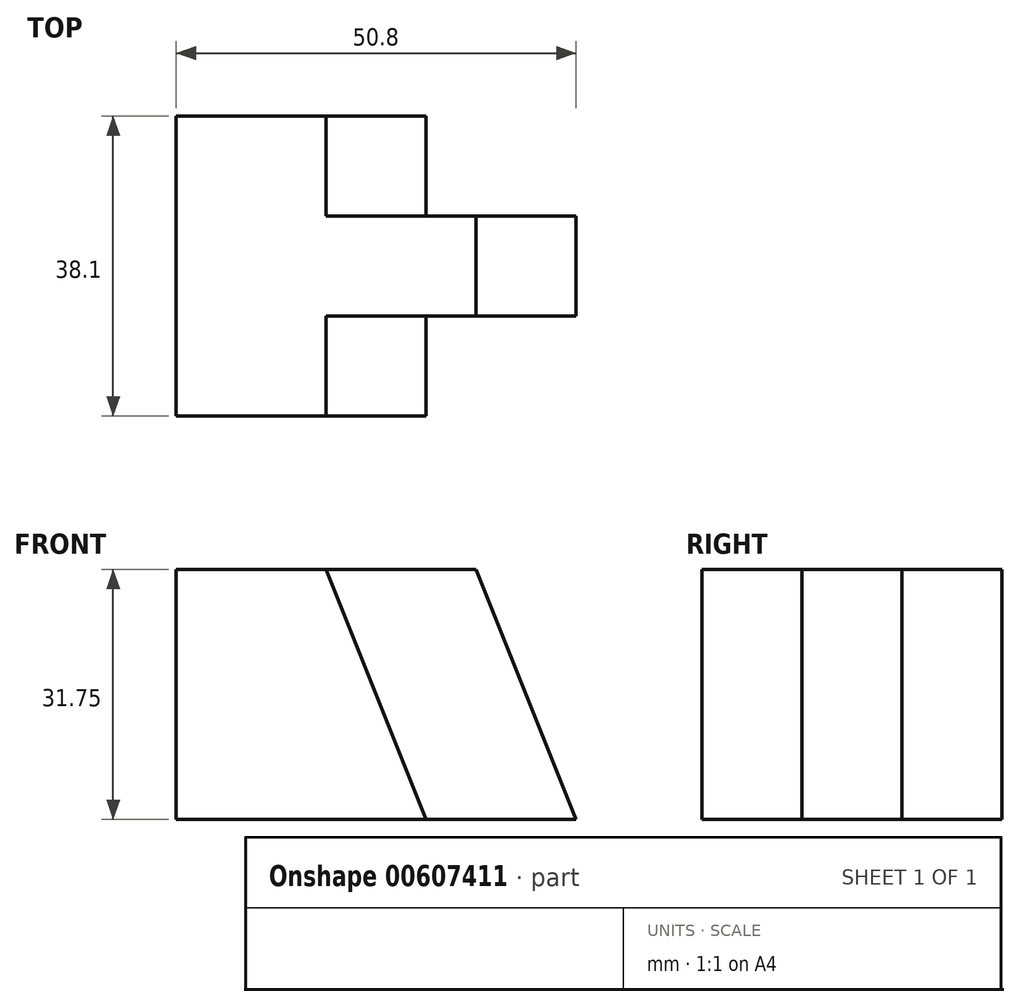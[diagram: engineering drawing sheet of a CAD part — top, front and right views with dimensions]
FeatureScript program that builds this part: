
annotation { "Feature Type Name" : "Feature", "Feature Type Description" : "" }
export const myFeature = defineFeature(function(context is Context, id is Id, definition is map)
    precondition{}
    {
        {
            var Q0;
            Q0=qCreatedBy(makeId("Right.planeOp"),FACE);
            var sketch = newSketch(context, id + "F0", { "sketchPlane" : qUnion([Q0])});
            skLineSegment(sketch, "E0", {"start": v(0, 0) * mm, "end": v(19.05, 0) * mm});
            skLineSegment(sketch, "E1", {"start": v(19.05, 0) * mm, "end": v(-19.05, 0) * mm});
            skLineSegment(sketch, "E2", {"start": v(-19.05, 0) * mm, "end": v(-19.05, -31.75) * mm});
            skLineSegment(sketch, "E3", {"start": v(-19.05, -31.75) * mm, "end": v(19.05, -31.75) * mm});
            skLineSegment(sketch, "E4", {"start": v(19.05, -31.75) * mm, "end": v(19.05, 0) * mm});
            skSolve(sketch);
        }
        {
            var Q0;
            Q0 = qSketchRegion(id + "F0", true);
            extrude(context, id + "F1", {"entities" : qUnion([Q0]), "depth" : 50.8 * mm, "offsetDistance" : 25.4 * mm});
        }
        {
            var Q0;
            Q0=makeQuery(id+"F1.opExtrude","CAP_FACE",FACE,{"disambiguationData":[OSD([sQuery(id+"F0.wireOp",EDGE,"E1"),sQuery(id+"F0.wireOp",EDGE,"E2"),sQuery(id+"F0.wireOp",EDGE,"E3"),sQuery(id+"F0.wireOp",EDGE,"E4")])],"isStart":false});
            var sketch = newSketch(context, id + "F2", { "sketchPlane" : qUnion([Q0])});
            skLineSegment(sketch, "E5", {"start": v(-19.05, 0) * mm, "end": v(-6.35, 0) * mm});
            skLineSegment(sketch, "E6", {"start": v(-6.35, 0) * mm, "end": v(-6.35, -31.75) * mm});
            skLineSegment(sketch, "E7", {"start": v(-6.35, -31.75) * mm, "end": v(-19.05, -31.75) * mm});
            skLineSegment(sketch, "E8", {"start": v(-19.05, -31.75) * mm, "end": v(-19.05, 0) * mm});
            skSolve(sketch);
        }
        {
            var Q0;
            Q0 = qSketchRegion(id + "F2", true);
            extrude(context, id + "F3", {"entities" : qUnion([Q0]), "operationType" : NewBodyOperationType.REMOVE, "oppositeDirection" : true, "depth" : 19.05 * mm, "offsetDistance" : 25.4 * mm});
        }
        {
            var Q0;
            Q0=makeQuery(id+"F1.opExtrude","SWEPT_FACE",FACE,{"disambiguationData":[OSD([sQuery(id+"F0.wireOp",EDGE,"E2")])]});
            var sketch = newSketch(context, id + "F4", { "sketchPlane" : qUnion([Q0])});
            skLineSegment(sketch, "E9", {"start": v(31.75, 0) * mm, "end": v(19.05, 0) * mm});
            skLineSegment(sketch, "E10", {"start": v(19.05, 0) * mm, "end": v(31.75, -31.75) * mm});
            skLineSegment(sketch, "E11", {"start": v(31.75, -31.75) * mm, "end": v(31.75, 0) * mm});
            skSolve(sketch);
        }
        {
            var Q0;
            Q0 = qSketchRegion(id + "F4", true);
            extrude(context, id + "F5", {"entities" : qUnion([Q0]), "operationType" : NewBodyOperationType.REMOVE, "oppositeDirection" : true, "depth" : 12.7 * mm, "offsetDistance" : 25.4 * mm});
        }
        {
            var Q0;
            Q0=makeQuery(id+"F1.opExtrude","CAP_FACE",FACE,{"disambiguationData":[OSD([sQuery(id+"F0.wireOp",EDGE,"E1"),sQuery(id+"F0.wireOp",EDGE,"E2"),sQuery(id+"F0.wireOp",EDGE,"E3"),sQuery(id+"F0.wireOp",EDGE,"E4")])],"isStart":false});
            var sketch = newSketch(context, id + "F6", { "sketchPlane" : qUnion([Q0])});
            skLineSegment(sketch, "E12", {"start": v(6.35, 0) * mm, "end": v(6.35, -31.75) * mm});
            skLineSegment(sketch, "E13", {"start": v(6.35, -31.75) * mm, "end": v(19.05, -31.75) * mm});
            skLineSegment(sketch, "E14", {"start": v(19.05, -31.75) * mm, "end": v(19.05, 0) * mm});
            skLineSegment(sketch, "E15", {"start": v(19.05, 0) * mm, "end": v(6.35, 0) * mm});
            skSolve(sketch);
        }
        {
            var Q0;
            Q0 = qSketchRegion(id + "F6", true);
            extrude(context, id + "F7", {"entities" : qUnion([Q0]), "operationType" : NewBodyOperationType.REMOVE, "oppositeDirection" : true, "depth" : 19.05 * mm, "offsetDistance" : 25.4 * mm});
        }
        {
            var Q0;
            Q0=makeQuery(id+"F1.opExtrude","SWEPT_FACE",FACE,{"disambiguationData":[OSD([sQuery(id+"F0.wireOp",EDGE,"E4")])]});
            var sketch = newSketch(context, id + "F8", { "sketchPlane" : qUnion([Q0])});
            skLineSegment(sketch, "E16", {"start": v(-31.75, 0) * mm, "end": v(-19.05, 0) * mm});
            skLineSegment(sketch, "E17", {"start": v(-19.05, 0) * mm, "end": v(-31.75, -31.75) * mm});
            skLineSegment(sketch, "E18", {"start": v(-31.75, -31.75) * mm, "end": v(-31.75, 0) * mm});
            skSolve(sketch);
        }
        {
            var Q0;
            Q0 = qSketchRegion(id + "F8", true);
            extrude(context, id + "F9", {"entities" : qUnion([Q0]), "operationType" : NewBodyOperationType.REMOVE, "oppositeDirection" : true, "depth" : 12.7 * mm, "offsetDistance" : 25.4 * mm});
        }
        {
            var Q0;
            Q0=makeQuery(id+"F5.boolean.opBoolean","MERGE",FACE,{"derivedFrom":[makeQuery(id+"F3.boolean.opBoolean","COPY",FACE,{"derivedFrom":makeQuery(id+"F3.opExtrude","SWEPT_FACE",FACE,{"disambiguationData":[OSD([sQuery(id+"F2.wireOp",EDGE,"E6")])]})}),makeQuery(id+"F5.opExtrude","CAP_FACE",FACE,{"disambiguationData":[OSD([sQuery(id+"F4.wireOp",EDGE,"E9"),sQuery(id+"F4.wireOp",EDGE,"E10"),sQuery(id+"F4.wireOp",EDGE,"E11")])],"isStart":false})]});
            var sketch = newSketch(context, id + "F10", { "sketchPlane" : qUnion([Q0])});
            skLineSegment(sketch, "E19", {"start": v(50.8, -31.75) * mm, "end": v(50.8, 0) * mm});
            skLineSegment(sketch, "E20", {"start": v(50.8, 0) * mm, "end": v(38.1, 0) * mm});
            skLineSegment(sketch, "E21", {"start": v(38.1, 0) * mm, "end": v(50.8, -31.75) * mm});
            skSolve(sketch);
        }
        {
            var Q0;
            Q0 = qSketchRegion(id + "F10", true);
            extrude(context, id + "F11", {"entities" : qUnion([Q0]), "operationType" : NewBodyOperationType.REMOVE, "oppositeDirection" : true, "depth" : 25.4 * mm, "offsetDistance" : 25.4 * mm});
        }
    });
